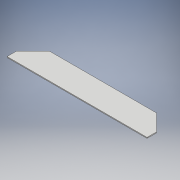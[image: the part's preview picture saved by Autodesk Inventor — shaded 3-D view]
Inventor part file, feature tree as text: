
AUTODESK INVENTOR PART (.ipt)
format: ipt  version: 2018 (Build 220112000, 112)  size: 104,960 bytes
history: native  units: mm
features: other x1, extrude x1, sketch x1
ambient origin geometry x8: Origin, YZ Plane, XZ Plane, XY Plane, X Axis, Y Axis, Z Axis, Center Point
bodies: Body1 (feature_tree)
feature tree (3):
  other  "ソリッド1"
  extrude  "押し出し1"  Depth=70.0mm
  sketch  "スケッチ1"
